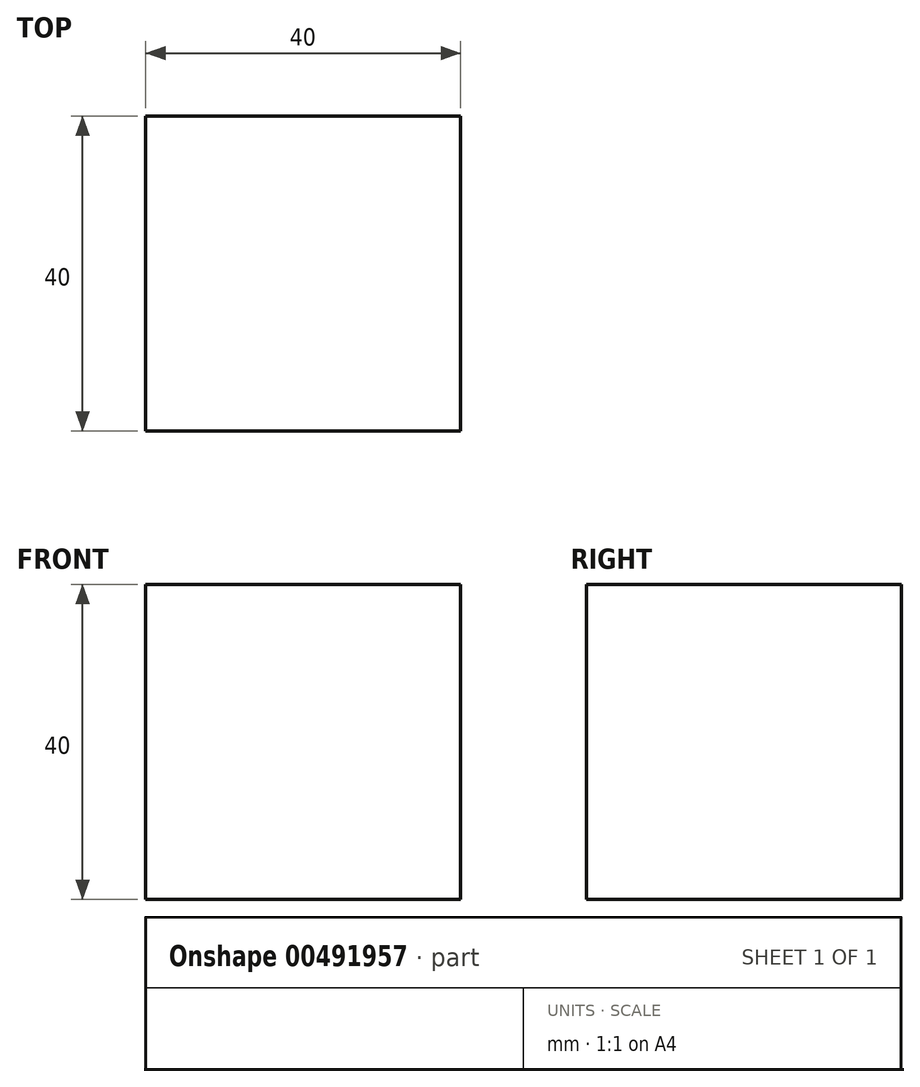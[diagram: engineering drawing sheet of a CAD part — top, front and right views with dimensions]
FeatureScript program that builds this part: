
annotation { "Feature Type Name" : "Feature", "Feature Type Description" : "" }
export const myFeature = defineFeature(function(context is Context, id is Id, definition is map)
    precondition{}
    {
        {
            var Q0;
            Q0=qCreatedBy(makeId("Top.planeOp"),FACE);
            var sketch = newSketch(context, id + "F0", { "sketchPlane" : qUnion([Q0])});
            skLineSegment(sketch, "E0.bottom", {"start": v(20, -20) * mm, "end": v(-20, -20) * mm});
            skLineSegment(sketch, "E0.top", {"start": v(20, 20) * mm, "end": v(-20, 20) * mm});
            skLineSegment(sketch, "E0.left", {"start": v(20, -20) * mm, "end": v(20, 20) * mm});
            skLineSegment(sketch, "E0.right", {"start": v(-20, -20) * mm, "end": v(-20, 20) * mm});
            skPoint(sketch, "E0.middle", {"position": v(0, 0) * mm});
            skSolve(sketch);
        }
        {
            var Q0;
            Q0=qSketchRegion(id+"F0",true);
            extrude(context, id + "F1", {"entities" : qUnion([Q0]), "depth" : 40 * mm});
        }
    });
